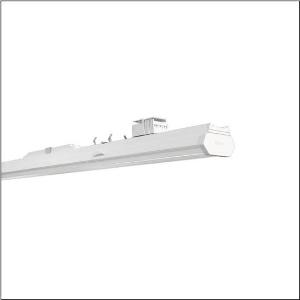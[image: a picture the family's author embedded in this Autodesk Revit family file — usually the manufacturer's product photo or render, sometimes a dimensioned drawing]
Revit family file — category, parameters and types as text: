
# Revit family: licross_r__11_protected_ho_51tp12dn4fxm3c_f4e0
name_source: partatom
category: Lighting Fixtures
units: mm (PartAtom-declared; Revit-internal decimal feet)

## family parameters
Cut with Voids When Loaded = No
Host = Face
Light Source = No
Part Type = Normal
Room Calculation Point = No
Round Connector Dimension = Use Diameter
Shared = No

## types (1)
- --- (1 x LED, 970 lm, 7.4 W, 4000K)
    Apparent Load = 7 VA
    CIE Flux Codes = 70 91 97 98 100
    Color Rendering = 80
    Color Temperature = 4000K
    Default Elevation = 1800 mm
    Description = Licross® 11 Protected HO, luminaire insert, of sheet steel, galvanised, coil coated, white, length: 1.500mm, width: 90mm, height: 101mm, LED rated luminous flux: 15.270lm, light colour: 840, control gear: DALI 2, with plug, 6-pole, with phase selection, for trunking rail, 14-core, mains connection: 220..240V, AC, 50/60Hz, rated input power: 91W, for trunking rail, 14-core, halogen-free wiring, for emergency light function, converter,control gear: single battery element, battery: LiFeP04, 9Ah, primary light control with lens, of plastic, primary optical cover: cover, of PMMA, light emission: direct distribution, primary light characteristic: symmetric, protection rating (complete): IP64, insulation class (complete): insulation class I (protective earthing), certification: CE, UKCA, protection symbol: D if used in an environment with conductive dust loads with corresponding accessories, impact resistance: IK06, permissible ambient temperature for indoor applications: +5..+30°C, standard: EN 60598-2-22, LABS conformity tested according to VDMA 24364:2018-05, reducing of maximum allowable ambient temperature of 5°C with ceiling mounting, corresponds to IFS (International Featured Standards) requirements for safety and quality in the food industry, packaging unit: 1 piece
    Height = 92 mm
    Lamp = 1 x LED
    Lamp Light Flux = 970 lm
    Lamp Power = 7.4 W
    Lamp count = 1
    Length = 1500 mm
    Luminous efficacy = 131 lm/W
    Manufacturer = Siteco
    ModVariant = No
    Model = 51TP12DN4FXM3C
    Mounting Place = Ceiling
    Mounting Type = Pendant
    Number of Poles = 1
    OnlyDefault = Yes
    Power Factor = 1
    Product Name = Licross® 11 Protected HO
    Product group = luminaire insert
    ProductGroupID = 901
    Protection Class = Protection class I
    Protection Degree = IP 64
    RLX_Detail_Level = 1
    RLX_Emergency_Light_Flux = 0 lm
    RLX_Emergency_Type = 0
    RLX_Emergency_Type_DB = No
    RlxData = <blob elided: 24949 chars, md5=e950a624>
    Socket = socket
    Standby Power = 0 W
    System Light Flux = 970 lm
    System Power = 7 W
    Type Comments = : emergency light operation: 3 h
    Type Image = l_1256148.jpg
    URL = http://relux.com
    VarID = @adj_041479
    Voltage = 0 V
    Weight = 0.00 kg
    Width = 88 mm

## geometry (parser evidence)
native form markers: Blend x4, Sweep x10
no freeform markers — native parametric forms only
